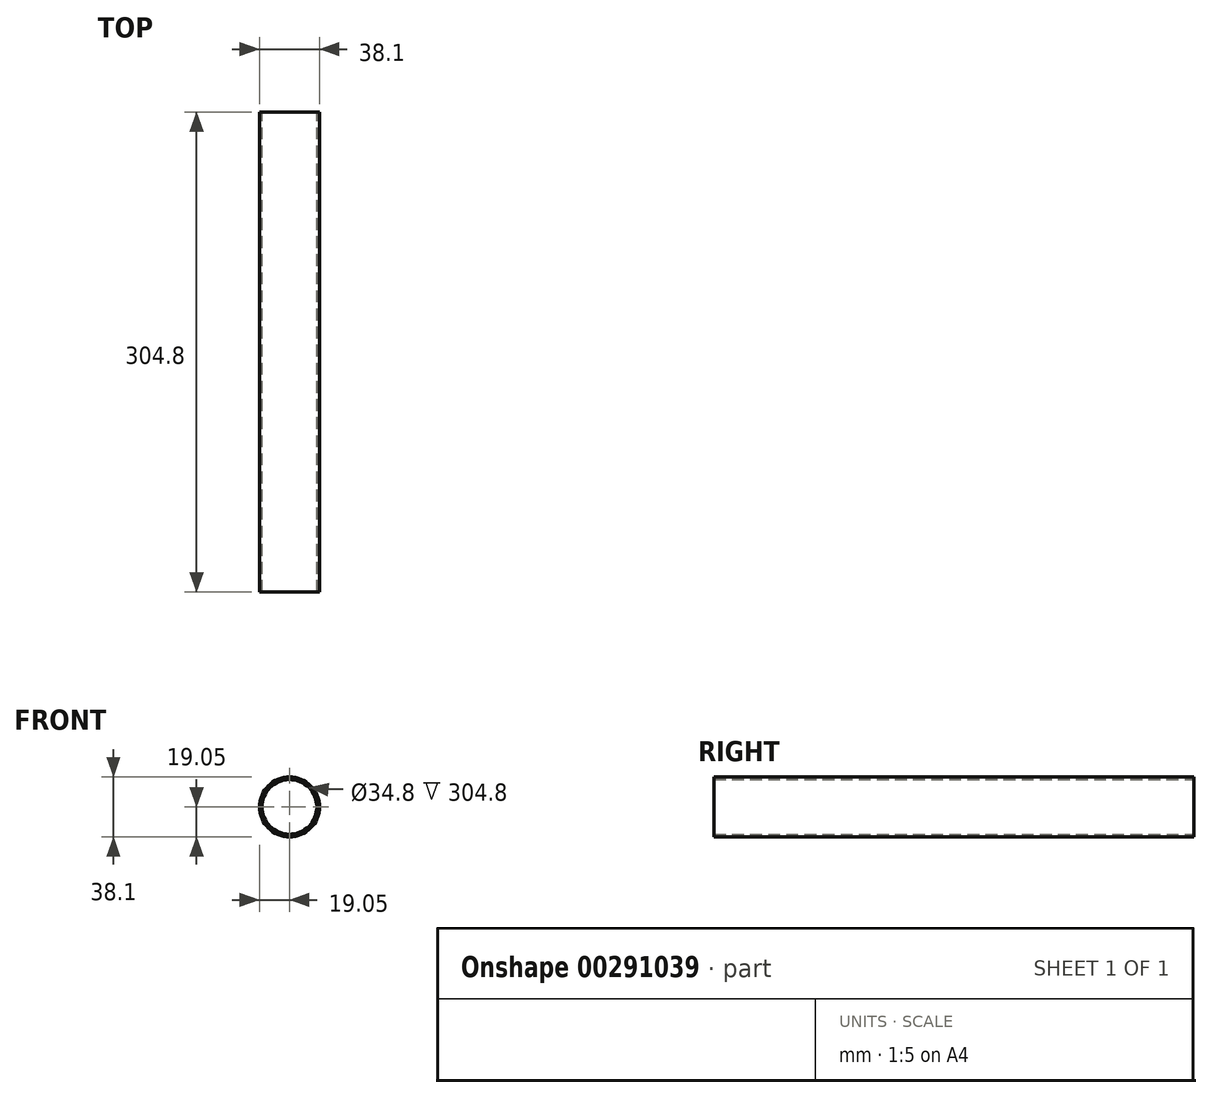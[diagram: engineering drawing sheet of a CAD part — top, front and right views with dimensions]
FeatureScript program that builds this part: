
annotation { "Feature Type Name" : "Feature", "Feature Type Description" : "" }
export const myFeature = defineFeature(function(context is Context, id is Id, definition is map)
    precondition{}
    {
        {
            var Q0;
            Q0=qCreatedBy(makeId("Front.planeOp"),FACE);
            var sketch = newSketch(context, id + "F0", { "sketchPlane" : qUnion([Q0])});
            skCircle(sketch, "E0", {"center": v(0, 0) * mm, "radius": 38.1 * mm});
            skCircle(sketch, "E1", {"center": v(0, 0) * mm, "radius": 36.45 * mm});
            skLineSegment(sketch, "E2.bottom", {"start": v(-13.34, 95.25) * mm, "end": v(13.34, 95.25) * mm});
            skLineSegment(sketch, "E2.top", {"start": v(-13.34, 31.75) * mm, "end": v(13.34, 31.75) * mm});
            skLineSegment(sketch, "E2.left", {"start": v(-13.34, 95.25) * mm, "end": v(-13.34, 31.75) * mm});
            skLineSegment(sketch, "E2.right", {"start": v(13.33, 95.25) * mm, "end": v(13.33, 31.75) * mm});
            skLineSegment(sketch, "E3", {"start": v(0, 31.75) * mm, "end": v(0, 0) * mm, "construction": true});
            skCircle(sketch, "E4", {"center": v(0, 19.05) * mm, "radius": 19.05 * mm});
            skCircle(sketch, "E5", {"center": v(0, 19.05) * mm, "radius": 17.4 * mm});
            skPoint(sketch, "E6", {"position": v(0, 38.1) * mm});
            skCircle(sketch, "E7", {"center": v(0, 31.75) * mm, "radius": 13.33 * mm});
            skSolve(sketch);
        }
        {
            var Q0;
            Q0=qCreatedBy(makeId("Front.planeOp"),FACE);
            var sketch = newSketch(context, id + "F1", { "sketchPlane" : qUnion([Q0])});
            skCircle(sketch, "E8.0", {"center": v(0, 19.05) * mm, "radius": 19.05 * mm});
            skCircle(sketch, "E9.0", {"center": v(0, 19.05) * mm, "radius": 17.4 * mm});
            skSolve(sketch);
        }
        {
            var Q0;
            Q0 = qSketchRegion(id + "F1", true);
            extrude(context, id + "F2", {"entities" : qUnion([Q0]), "endBound" : BoundingType.SYMMETRIC, "depth" : 304.8 * mm});
        }
    });
